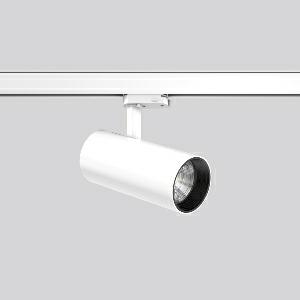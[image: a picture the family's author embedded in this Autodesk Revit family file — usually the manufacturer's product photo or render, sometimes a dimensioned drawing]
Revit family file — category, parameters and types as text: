
# Revit family: deecos_s_mini_742194_002_1_76_6b29
name_source: partatom
category: Lighting Fixtures
units: mm (PartAtom-declared; Revit-internal decimal feet)

## family parameters
Cut with Voids When Loaded = No
Host = Face
Light Source = No
Part Type = Normal
Room Calculation Point = No
Round Connector Dimension = Use Diameter
Shared = No

## types (1)
- DEECOS S mini (1 x LED Modul 940, 2250 lm, 4000)
    Apparent Load = 22 VA
    Approval mark = CE
    CIE Flux Codes = 99 100 100 100 100
    Color Rendering = 92
    Color Temperature = 4000
    Default Elevation = 1800 mm
    Description = Series: DEECOS S mini
LED surface-mounted projector in modern design with no visible cooling ribs. Housing: die-cast aluminium, powder-coated. Rotation range: 356°. Swivel range: 90°. Black plastic ring and recessed LED to prevent glare from the side. Optical assembly with lens made of plastic (polycarbonate) for the best homogeneous light distribution - can be changed without tools. Best colour rendering index Ra>90. Superspot version with small spot LED. With adapter for RZB 3-circuit DALI tracks. Suitable for Track on ceiling, Wall track. High quality converter without flickering and stroboscopic effect. The following accessories can be mounted without use of tools: interchangeable lenses, decorative glasses, honeycomb louvre, clear and frosted diffusers, white interchangeable plastic ring. 
Colour: traffic white, matt (RAL 9016)
Diameter: 87 mm
Height: 214 mm
Lamp: LED
Socket: without socket
Colour temperature: 4000K
Colour rendering index (CRI): 92
System power: 22 W
Rated luminous flux: 2250 lm
Luminous efficiency: 102 lm/W
Control gear: Converter, dimmable, DALI
Protection class: I
Type of protection: IP 20
    Height = 214 mm
    Lamp = 1 x LED Modul 940
    Lamp Light Flux = 2250 lm
    Lamp count = 1
    Length = 87 mm
    Lifetime = 50000 h
    Luminous efficacy = 102 lm/W
    Manufacturer = RZB
    ModVariant = No
    Model = 742194.002.1.76
    Mounting Place = Ceiling
    Mounting Type = Rail mounted
    Number of Poles = 1
    OnlyDefault = Yes
    Power Factor = 1
    Product Name = DEECOS S mini
    Product group = Track mounted projectors
    ProductGroupID = 301
    Protection Class = Protection class I
    Protection Degree = IP 20
    RLX_Detail_Level = 1
    RLX_Emergency_Light_Flux = 0 lm
    RLX_Emergency_Type = 0
    RLX_Emergency_Type_DB = No
    RlxData = <blob elided: 35573 chars, md5=24ad465a>
    Socket = socket
    Standby Power = 0 W
    System Light Flux = 2250 lm
    System Power = 22 W
    Type Comments = Product without accessories
    Type Image = 741930.002.jpg
    URL = http://relux.com
    VarID = ---
    Voltage = 230 V
    Voltage Range = 220-240 V
    Weight = 0.00 kg
    Width = 0 mm  [stored 0 ft]

note: [stored X ft] marks values corroborated as IEEE doubles in the binary element streams (Revit-internal decimal feet)

## geometry (parser evidence)
native form markers: Blend x4, Sweep x13
no freeform markers — native parametric forms only
